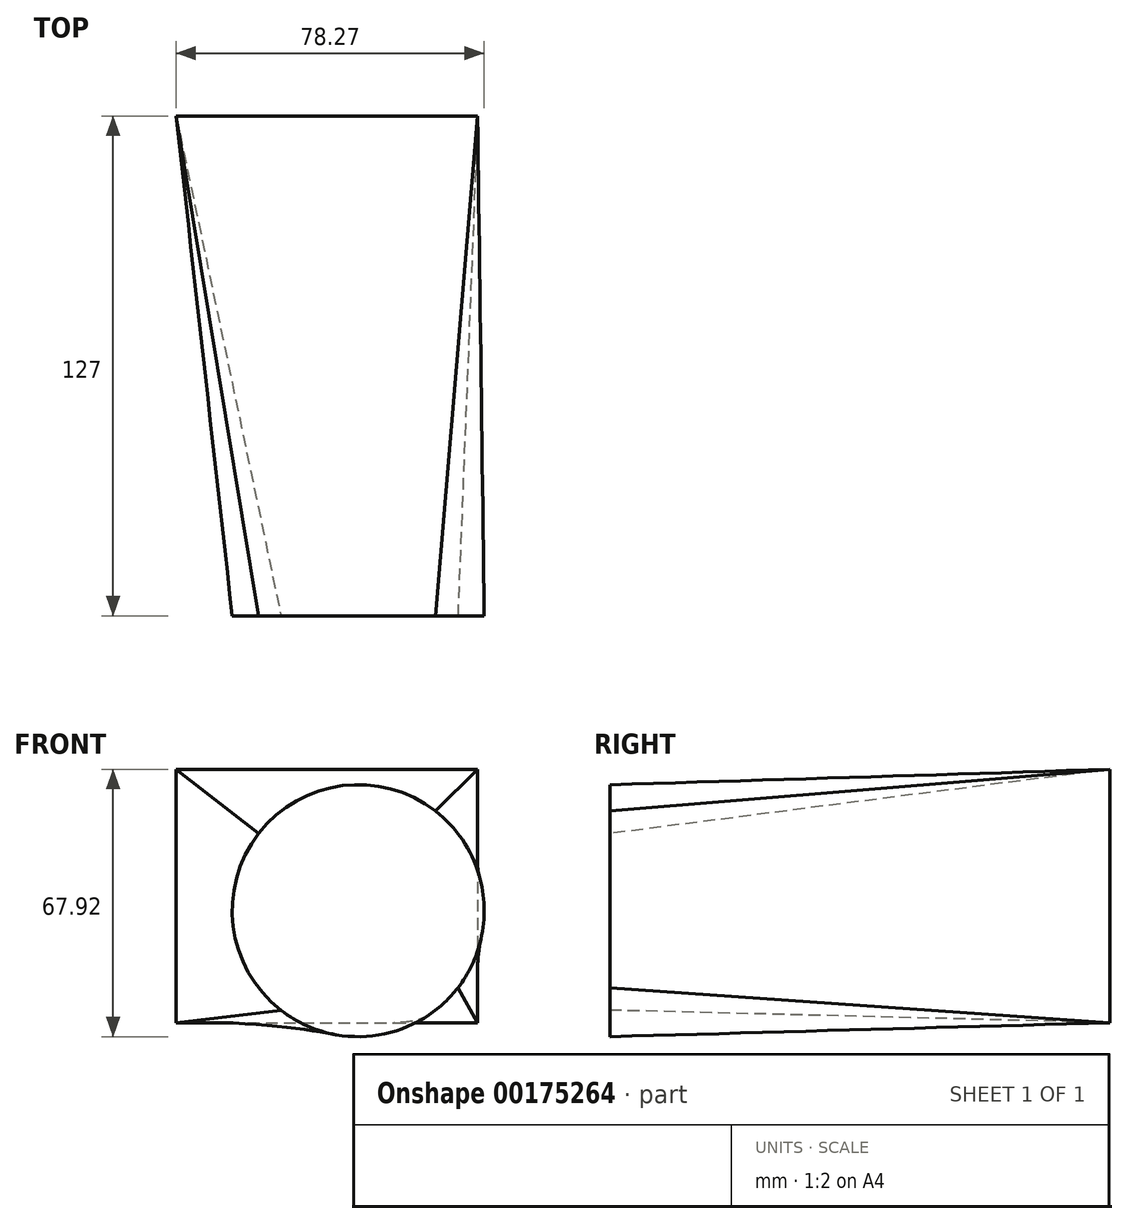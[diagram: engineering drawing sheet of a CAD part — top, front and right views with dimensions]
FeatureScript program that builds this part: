
annotation { "Feature Type Name" : "Feature", "Feature Type Description" : "" }
export const myFeature = defineFeature(function(context is Context, id is Id, definition is map)
    precondition{}
    {
        {
            var Q0;
            Q0=qCreatedBy(makeId("Front.planeOp"),FACE);
            var sketch = newSketch(context, id + "F0", { "sketchPlane" : qUnion([Q0])});
            skLineSegment(sketch, "E0.bottom", {"start": v(-34.57, 35.9) * mm, "end": v(42.02, 35.9) * mm});
            skLineSegment(sketch, "E0.top", {"start": v(-34.57, -28.46) * mm, "end": v(42.02, -28.46) * mm});
            skLineSegment(sketch, "E0.left", {"start": v(-34.57, 35.9) * mm, "end": v(-34.57, -28.46) * mm});
            skLineSegment(sketch, "E0.right", {"start": v(42.02, 35.9) * mm, "end": v(42.02, -28.46) * mm});
            skSolve(sketch);
        }
        {
            var Q0;
            Q0=qCreatedBy(makeId("Front.planeOp"),FACE);
            cPlane(context, id + "F1", {"entities" : qUnion([Q0]), "cplaneType" : CPlaneType.OFFSET, "offset" : 127 * mm, "width" : 152.4 * mm, "height" : 152.4 * mm});
        }
        {
            var Q0;
            Q0=qCreatedBy(id+"F1.planeOp",FACE);
            var sketch = newSketch(context, id + "F2", { "sketchPlane" : qUnion([Q0])});
            skCircle(sketch, "E1", {"center": v(11.7, 0) * mm, "radius": 32 * mm});
            skSolve(sketch);
        }
        {
            var Q0;
            Q0=makeQuery(id+"F0.imprint","IMPRINT",FACE,{"disambiguationData":[TD([[makeQuery(id+"F0.imprint","IMPRINT",EDGE,{"derivedFrom":sQuery(id+"F0.wireOp",EDGE,"E0.bottom")}),-1.0]])]});
            var Q1;
            Q1=makeQuery(id+"F2.imprint","IMPRINT",FACE,{"disambiguationData":[TD([[makeQuery(id+"F2.imprint","IMPRINT",EDGE,{"derivedFrom":sQuery(id+"F2.wireOp",EDGE,"E1")}),1.0]])]});
            loft(context, id + "F3", {"sheetProfilesArray" : [{ "sheetProfileEntities" : qUnion([Q0]) }, { "sheetProfileEntities" : qUnion([Q1]) }]});
        }
    });
